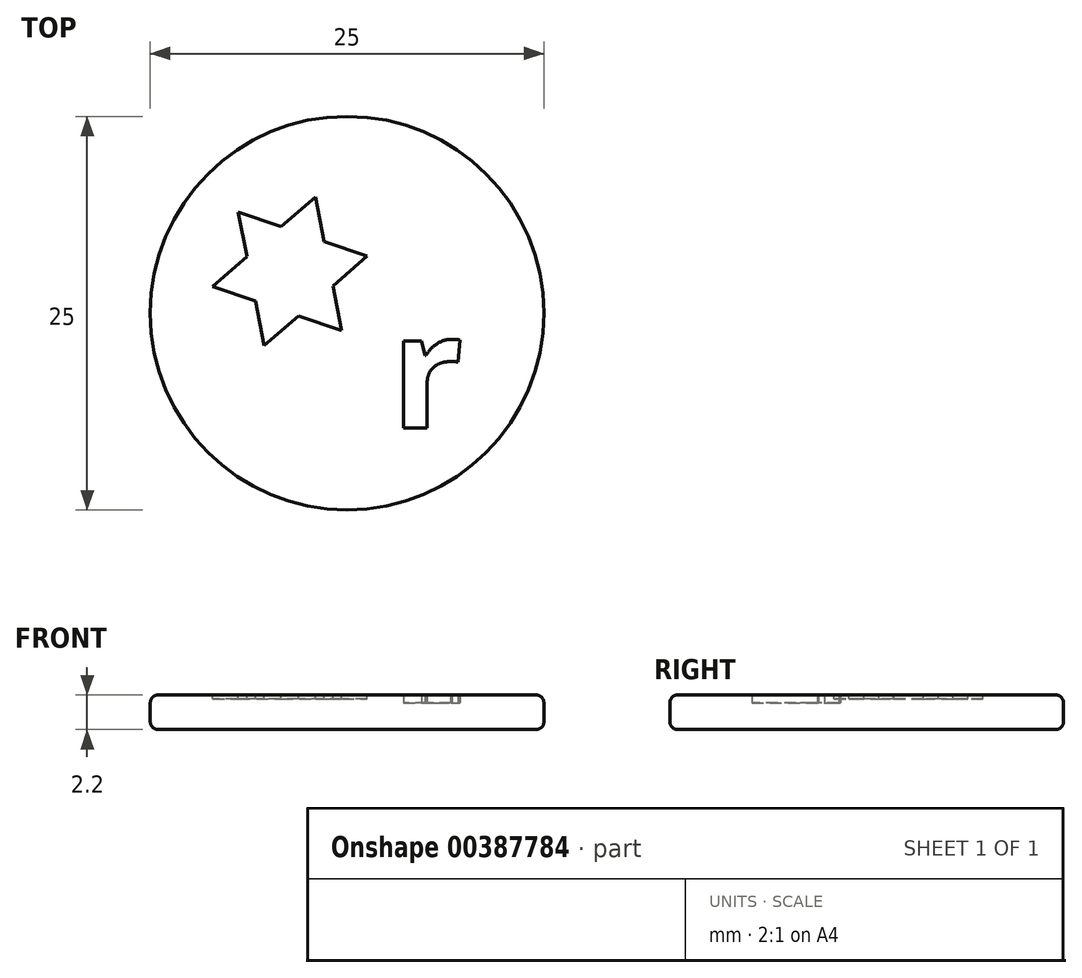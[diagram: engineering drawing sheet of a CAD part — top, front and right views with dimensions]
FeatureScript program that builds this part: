
annotation { "Feature Type Name" : "Feature", "Feature Type Description" : "" }
export const myFeature = defineFeature(function(context is Context, id is Id, definition is map)
    precondition{}
    {
        {
            var Q0;
            Q0=qCreatedBy(makeId("Top.planeOp"),FACE);
            var sketch = newSketch(context, id + "F0", { "sketchPlane" : qUnion([Q0])});
            skCircle(sketch, "E0", {"center": v(0, 0) * mm, "radius": 12.5 * mm});
            skSolve(sketch);
        }
        {
            var Q0;
            Q0=makeQuery(id+"F0.imprint","IMPRINT",FACE,{"disambiguationData":[TD([[makeQuery(id+"F0.imprint","IMPRINT",EDGE,{"derivedFrom":sQuery(id+"F0.wireOp",EDGE,"E0")}),1.0]])]});
            extrude(context, id + "F1", {"entities" : qUnion([Q0]), "depth" : 2.2 * mm});
        }
        {
            var Q0;
            Q0=makeQuery(id+"F1.opExtrude","CAP_FACE",FACE,{"disambiguationData":[OSD([sQuery(id+"F0.wireOp",EDGE,"E0")])],"isStart":false});
            var Q1;
            Q1=makeQuery(id+"F1.opExtrude","CAP_EDGE",EDGE,{"disambiguationData":[OSD([sQuery(id+"F0.wireOp",EDGE,"E0")])],"isStart":false});
            fillet(context, id + "F2", {"entities" : qUnion([Q0, Q1]), "radius" : 0.5 * mm, "tangentPropagation" : true, "allowEdgeOverflow" : false});
        }
        {
            var Q0;
            Q0=makeQuery(id+"F1.opExtrude","CAP_FACE",FACE,{"disambiguationData":[OSD([sQuery(id+"F0.wireOp",EDGE,"E0")])],"isStart":true});
            fillet(context, id + "F3", {"entities" : qUnion([Q0]), "radius" : 0.5 * mm, "tangentPropagation" : true, "allowEdgeOverflow" : false});
        }
        {
            var Q0;
            Q0=makeQuery(id+"F1.opExtrude","CAP_FACE",FACE,{"disambiguationData":[OSD([sQuery(id+"F0.wireOp",EDGE,"E0")])],"isStart":false});
            var sketch = newSketch(context, id + "F4", { "sketchPlane" : qUnion([Q0])});
            skCircle(sketch, "E1.cCircle", {"center": v(-3.63, 2.66) * mm, "radius": 5 * mm, "construction": true});
            skLineSegment(sketch, "E1.0", {"start": v(-0.35, -1.11) * mm, "end": v(-8.54, 1.7) * mm});
            skLineSegment(sketch, "E1.1", {"start": v(-8.54, 1.7) * mm, "end": v(-2, 7.39) * mm});
            skLineSegment(sketch, "E1.2", {"start": v(-2, 7.39) * mm, "end": v(-0.35, -1.11) * mm});
            skLineSegment(sketch, "E2.0", {"start": v(-5.26, -2.07) * mm, "end": v(-6.91, 6.43) * mm});
            skLineSegment(sketch, "E2.1", {"start": v(-6.91, 6.43) * mm, "end": v(1.28, 3.61) * mm});
            skLineSegment(sketch, "E2.2", {"start": v(1.28, 3.61) * mm, "end": v(-5.26, -2.07) * mm});
            skSolve(sketch);
        }
        {
            var Q0;
            Q0 = qSketchRegion(id + "F4", true);
            extrude(context, id + "F5", {"entities" : qUnion([Q0]), "operationType" : NewBodyOperationType.REMOVE, "endBound" : BoundingType.SYMMETRIC, "oppositeDirection" : true, "depth" : 0.5 * mm});
        }
        {
            var Q0;
            Q0=makeQuery(id+"F1.opExtrude","CAP_FACE",FACE,{"disambiguationData":[OSD([sQuery(id+"F0.wireOp",EDGE,"E0")])],"isStart":false});
            var sketch = newSketch(context, id + "F6", { "sketchPlane" : qUnion([Q0])});
            skText(sketch, "E3", { "text": "r", "fontName": "OpenSans-Bold.ttf"});
            const initialGuessF6  = {"E3": [0.00278, -0.0073, 1, 0, 0.0073]};
            skSetInitialGuess(sketch, initialGuessF6);
            skSolve(sketch);
        }
        {
            var Q0;
            Q0 = qSketchRegion(id + "F6", true);
            extrude(context, id + "F7", {"entities" : qUnion([Q0]), "operationType" : NewBodyOperationType.REMOVE, "endBound" : BoundingType.SYMMETRIC, "depth" : 1 * mm});
        }
    });
